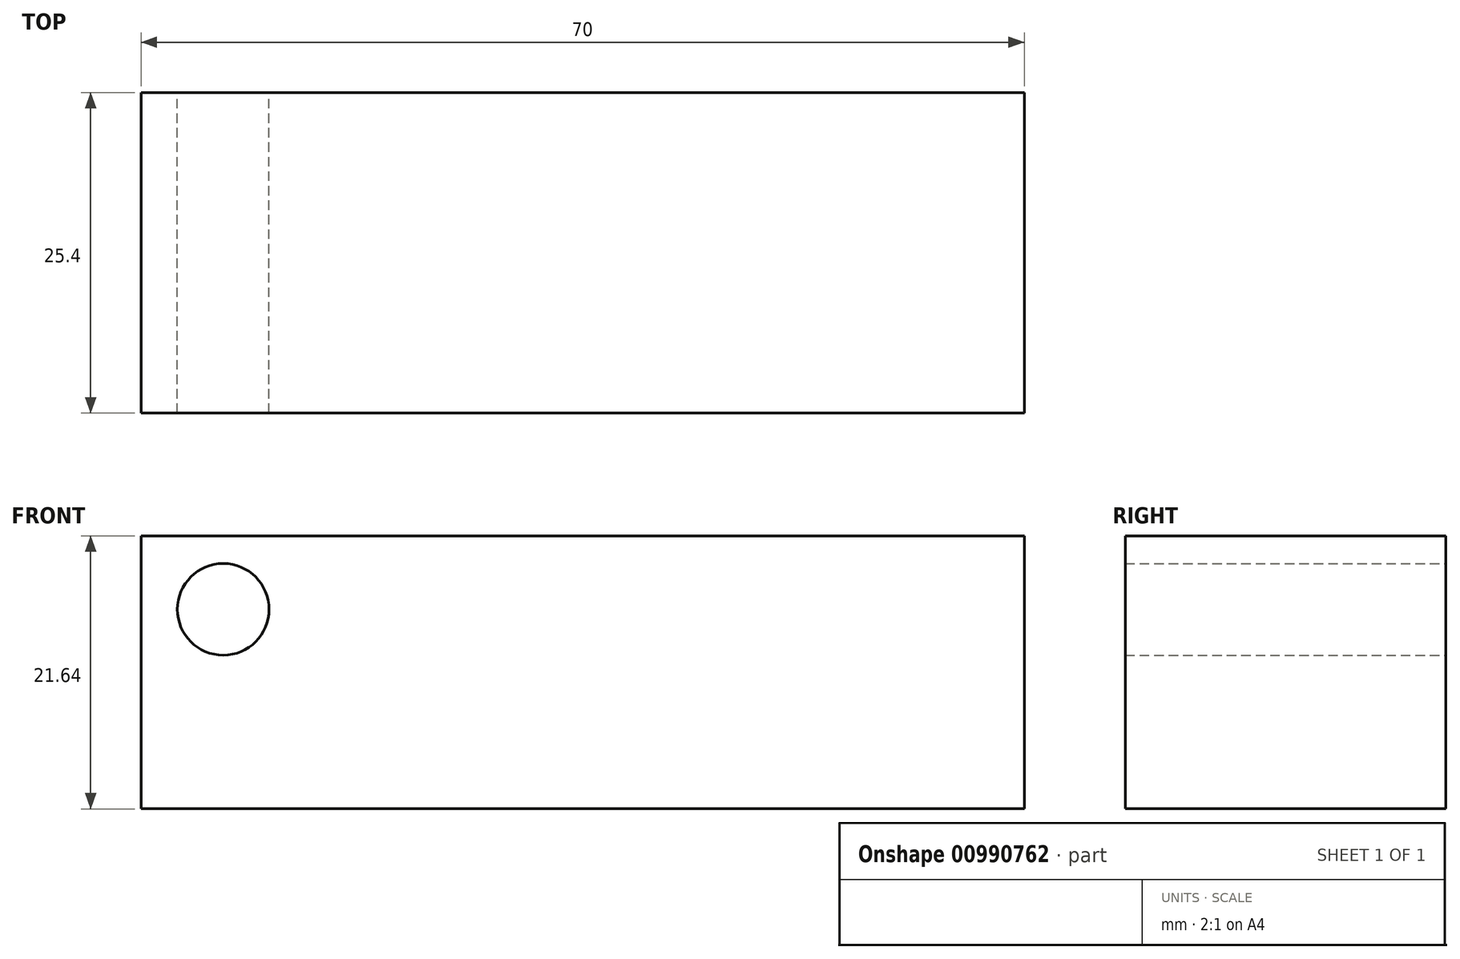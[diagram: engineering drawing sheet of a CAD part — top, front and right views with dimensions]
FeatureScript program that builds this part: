
annotation { "Feature Type Name" : "Feature", "Feature Type Description" : "" }
export const myFeature = defineFeature(function(context is Context, id is Id, definition is map)
    precondition{}
    {
        {
            var Q0;
            Q0=qCreatedBy(makeId("Front.planeOp"),FACE);
            var sketch = newSketch(context, id + "F0", { "sketchPlane" : qUnion([Q0])});
            skLineSegment(sketch, "E0.bottom", {"start": v(35, -10.82) * mm, "end": v(-35, -10.82) * mm});
            skLineSegment(sketch, "E0.top", {"start": v(35, 10.82) * mm, "end": v(-35, 10.82) * mm});
            skLineSegment(sketch, "E0.left", {"start": v(35, -10.82) * mm, "end": v(35, 10.82) * mm});
            skLineSegment(sketch, "E0.right", {"start": v(-35, -10.82) * mm, "end": v(-35, 10.82) * mm});
            skPoint(sketch, "E0.middle", {"position": v(0, 0) * mm});
            skSolve(sketch);
        }
        {
            var Q0;
            Q0=makeQuery(id+"F0.imprint","IMPRINT",FACE,{"disambiguationData":[TD([[makeQuery(id+"F0.imprint","IMPRINT",EDGE,{"derivedFrom":sQuery(id+"F0.wireOp",EDGE,"E0.bottom")}),-1.0]])]});
            extrude(context, id + "F1", {"entities" : qUnion([Q0]), "depth" : 25.4 * mm, "offsetDistance" : 25.4 * mm});
        }
        {
            var Q0;
            Q0=qCreatedBy(makeId("Front.planeOp"),FACE);
            var sketch = newSketch(context, id + "F2", { "sketchPlane" : qUnion([Q0])});
            skCircle(sketch, "E1", {"center": v(-28.5, 5) * mm, "radius": 3.63 * mm});
            skSolve(sketch);
        }
        {
            var Q0;
            Q0=makeQuery(id+"F2.imprint","IMPRINT",FACE,{"disambiguationData":[TD([[makeQuery(id+"F2.imprint","IMPRINT",EDGE,{"derivedFrom":sQuery(id+"F2.wireOp",EDGE,"E1")}),1.0]])]});
            extrude(context, id + "F3", {"entities" : qUnion([Q0]), "depth" : 25.4 * mm, "offsetDistance" : 25.4 * mm});
        }
    });
